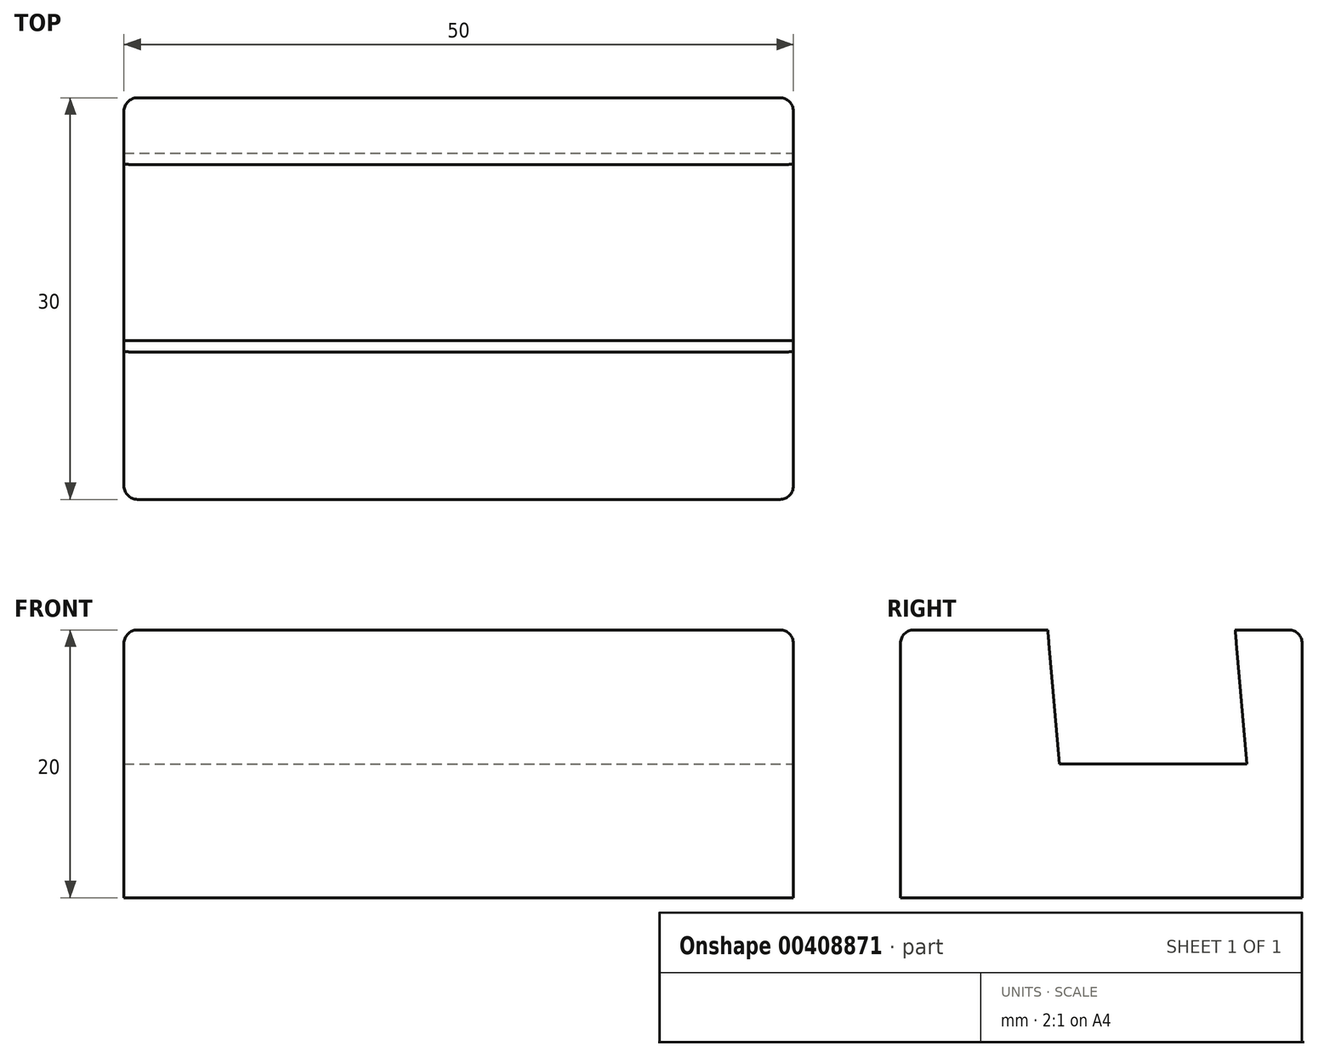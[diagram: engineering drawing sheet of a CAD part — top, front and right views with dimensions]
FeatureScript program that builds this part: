
annotation { "Feature Type Name" : "Feature", "Feature Type Description" : "" }
export const myFeature = defineFeature(function(context is Context, id is Id, definition is map)
    precondition{}
    {
        {
            var Q0;
            Q0=qCreatedBy(makeId("Right.planeOp"),FACE);
            var sketch = newSketch(context, id + "F0", { "sketchPlane" : qUnion([Q0])});
            skLineSegment(sketch, "E0.bottom", {"start": v(-15, 0) * mm, "end": v(15, 0) * mm});
            skLineSegment(sketch, "E0.top", {"start": v(-15, 20) * mm, "end": v(15, 20) * mm});
            skLineSegment(sketch, "E0.left", {"start": v(-15, 0) * mm, "end": v(-15, 20) * mm});
            skLineSegment(sketch, "E0.right", {"start": v(15, 0) * mm, "end": v(15, 20) * mm});
            skSolve(sketch);
        }
        {
            var Q0;
            Q0=makeQuery(id+"F0.imprint","IMPRINT",FACE,{"disambiguationData":[TD([[makeQuery(id+"F0.imprint","IMPRINT",EDGE,{"derivedFrom":sQuery(id+"F0.wireOp",EDGE,"E0.bottom")}),1.0]])]});
            extrude(context, id + "F1", {"entities" : qUnion([Q0]), "endBound" : BoundingType.SYMMETRIC, "depth" : 50 * mm});
        }
        {
            var Q0;
            Q0=makeQuery(id+"F1.opExtrude","CAP_FACE",FACE,{"disambiguationData":[OSD([sQuery(id+"F0.wireOp",EDGE,"E0.bottom"),sQuery(id+"F0.wireOp",EDGE,"E0.top"),sQuery(id+"F0.wireOp",EDGE,"E0.left"),sQuery(id+"F0.wireOp",EDGE,"E0.right")])],"isStart":false});
            var sketch = newSketch(context, id + "F2", { "sketchPlane" : qUnion([Q0])});
            skLineSegment(sketch, "E1.0.0", {"start": v(15, 20) * mm, "end": v(-15, 20) * mm});
            skLineSegment(sketch, "E1.0.1", {"start": v(-15, 20) * mm, "end": v(-15, 0) * mm});
            skLineSegment(sketch, "E1.0.2", {"start": v(-15, 0) * mm, "end": v(15, 0) * mm});
            skLineSegment(sketch, "E1.0.3", {"start": v(15, 0) * mm, "end": v(15, 20) * mm});
            skLineSegment(sketch, "E2", {"start": v(-4, 20) * mm, "end": v(-3.13, 10) * mm});
            skLineSegment(sketch, "E3", {"start": v(-3.13, 10) * mm, "end": v(10.87, 10) * mm});
            skLineSegment(sketch, "E4", {"start": v(10.87, 10) * mm, "end": v(10, 20) * mm});
            skLineSegment(sketch, "E5", {"start": v(10, 20) * mm, "end": v(-4, 20) * mm});
            skSolve(sketch);
        }
        {
            var Q0;
            Q0=makeQuery(id+"F2.imprint","IMPRINT",FACE,{"disambiguationData":[TD([[makeQuery(id+"F2.imprint","IMPRINT",EDGE,{"derivedFrom":sQuery(id+"F2.wireOp",EDGE,"E2")}),1.0]])]});
            extrude(context, id + "F3", {"entities" : qUnion([Q0]), "operationType" : NewBodyOperationType.REMOVE, "oppositeDirection" : true, "depth" : 50 * mm});
        }
        {
            var Q0;
            Q0=makeQuery(id+"F1.opExtrude","SWEPT_EDGE",EDGE,{"disambiguationData":[OSD([sQuery(id+"F0.wireOp",EDGE,"E0.top"),sQuery(id+"F0.wireOp",EDGE,"E0.left")])]});
            var Q1;
            {var subQ0=sQuery(id+"F0.wireOp",EDGE,"E0.left");var subQ1=sQuery(id+"F0.wireOp",EDGE,"E0.top");Q1=makeQuery(id+"F3.boolean.opBoolean","SPLIT",EDGE,{"disambiguationData":[TD([makeQuery(id+"F1.opExtrude","SWEPT_FACE",FACE,{"disambiguationData":[OSD([subQ0])]})])],"derivedFrom":makeQuery(id+"F1.opExtrude","CAP_EDGE",EDGE,{"disambiguationData":[OSD([subQ1])],"isStart":false})});}
            var Q2;
            {var subQ0=sQuery(id+"F0.wireOp",EDGE,"E0.right");var subQ1=sQuery(id+"F0.wireOp",EDGE,"E0.top");Q2=makeQuery(id+"F3.boolean.opBoolean","SPLIT",EDGE,{"disambiguationData":[TD([makeQuery(id+"F1.opExtrude","SWEPT_FACE",FACE,{"disambiguationData":[OSD([subQ0])]})])],"derivedFrom":makeQuery(id+"F1.opExtrude","CAP_EDGE",EDGE,{"disambiguationData":[OSD([subQ1])],"isStart":false})});}
            var Q3;
            Q3=makeQuery(id+"F1.opExtrude","SWEPT_EDGE",EDGE,{"disambiguationData":[OSD([sQuery(id+"F0.wireOp",EDGE,"E0.top"),sQuery(id+"F0.wireOp",EDGE,"E0.right")])]});
            var Q4;
            Q4=makeQuery(id+"F1.opExtrude","CAP_EDGE",EDGE,{"disambiguationData":[OSD([sQuery(id+"F0.wireOp",EDGE,"E0.right")])],"isStart":false});
            var Q5;
            Q5=makeQuery(id+"F1.opExtrude","CAP_EDGE",EDGE,{"disambiguationData":[OSD([sQuery(id+"F0.wireOp",EDGE,"E0.left")])],"isStart":false});
            var Q6;
            Q6=makeQuery(id+"F1.opExtrude","CAP_EDGE",EDGE,{"disambiguationData":[OSD([sQuery(id+"F0.wireOp",EDGE,"E0.left")])],"isStart":true});
            var Q7;
            {var subQ0=sQuery(id+"F0.wireOp",EDGE,"E0.left");var subQ1=sQuery(id+"F0.wireOp",EDGE,"E0.top");Q7=makeQuery(id+"F3.boolean.opBoolean","SPLIT",EDGE,{"disambiguationData":[TD([makeQuery(id+"F1.opExtrude","SWEPT_FACE",FACE,{"disambiguationData":[OSD([subQ0])]})])],"derivedFrom":makeQuery(id+"F1.opExtrude","CAP_EDGE",EDGE,{"disambiguationData":[OSD([subQ1])],"isStart":true})});}
            var Q8;
            Q8=makeQuery(id+"F1.opExtrude","CAP_EDGE",EDGE,{"disambiguationData":[OSD([sQuery(id+"F0.wireOp",EDGE,"E0.right")])],"isStart":true});
            var Q9;
            {var subQ0=sQuery(id+"F0.wireOp",EDGE,"E0.right");var subQ1=sQuery(id+"F0.wireOp",EDGE,"E0.top");Q9=makeQuery(id+"F3.boolean.opBoolean","SPLIT",EDGE,{"disambiguationData":[TD([makeQuery(id+"F1.opExtrude","SWEPT_FACE",FACE,{"disambiguationData":[OSD([subQ0])]})])],"derivedFrom":makeQuery(id+"F1.opExtrude","CAP_EDGE",EDGE,{"disambiguationData":[OSD([subQ1])],"isStart":true})});}
            fillet(context, id + "F4", {"entities" : qUnion([Q0, Q1, Q2, Q3, Q4, Q5, Q6, Q7, Q8, Q9]), "radius" : 1 * mm, "tangentPropagation" : true, "allowEdgeOverflow" : false});
        }
    });
